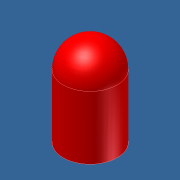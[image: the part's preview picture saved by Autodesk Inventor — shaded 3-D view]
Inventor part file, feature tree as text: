
AUTODESK INVENTOR PART (.ipt)
format: ipt  version: unknown  size: 174,592 bytes
history: native  units: mm
features: extrude x1, fillet x1, sketch x1
ambient origin geometry x8: Origin, YZ Plane, XZ Plane, XY Plane, X Axis, Y Axis, Z Axis, Center Point
feature tree (3):
  extrude  "Выдавливание1"  Depth=3.0mm
  fillet  "Сопряжение1"  Radius=5.0mm
  sketch  "Эскиз1"
